# Revit family: LENSES-PDI1000xWSxBx
name_source: partatom
category: Leuchten
units: mm (PartAtom-declared; Revit-internal decimal feet)

## family parameters
Basisbauteil = Fläche
Beim Laden mit Abzugskörper schneiden = Nein
Bemaßung runder Anschluss = Durchmesser verwenden
Gemeinsam genutzt = Nein
Lichtquelle = Ja
OmniClass-Nummer = 23.80.70.11
OmniClass-Titel = Luminaries for Internal Lighting
Raumberechnungspunkt = Nein
Teiletyp = Normal

## types (6) — shared parameters
Baugruppenkennzeichen = D5020200
Datei für fotometrisches Netz = LENSES_PDI.IES
Emissionsform beim Rendern sichtbar = Nein
Farbfilter = 16777215
Farbtemperaturverschiebung bei Dämpfen der Lampe = <Keine Auswahl>
Hersteller = RIDI Leuchten GmbH
Lampe = LED
Neigungswinkel = 90.00°
URL = www.ridi.de
Von Breite des Rechtecks ausssenden = 1019 mm
Von Länge des Rechtecks aussenden = 111 mm
brand = RIDI
conformity mark = CE
electrical safety class = 1
height = 35 mm  [stored 0.114829 ft]
ingress protection (IP) code = IP20
length = 1021 mm  [stored 3.34974 ft]
nominal frequency = 50-60Hz
nominal voltage = 230
voltage type (AC, DC, UC) = AC
weight = 2,8 kg
width = 113 mm  [stored 0.370735 ft]
zero-valued in all types: Vorgabe-Ansicht

## per-type parameters (varying)
| type | Modell | Scheinlast | rated input power |
| LENSES-PDI1000NDWS840B0500 | 0627808 | 32 VA | 32 |
| LENSES-PDI1000NDWS830B0500 | 0627809 | 32 VA | 32 |
| LENSES-PDI1000DAWS840B0500 | 0637808 | 32 VA | 32 |
| LENSES-PDI1000DAWS830B0500 | 0637809 | 32 VA | 32 |
| LENSES-PDI1000RFWS840B0600 | 0627864 | 37 VA | 37 |
| LENSES-PDI1000RFWS830B0550 | 0627865 | 37 VA | 37 |

note: column(s) folded — value = type name in every type: product name

note: [stored X ft] marks values corroborated as IEEE doubles in the binary element streams (Revit-internal decimal feet)
